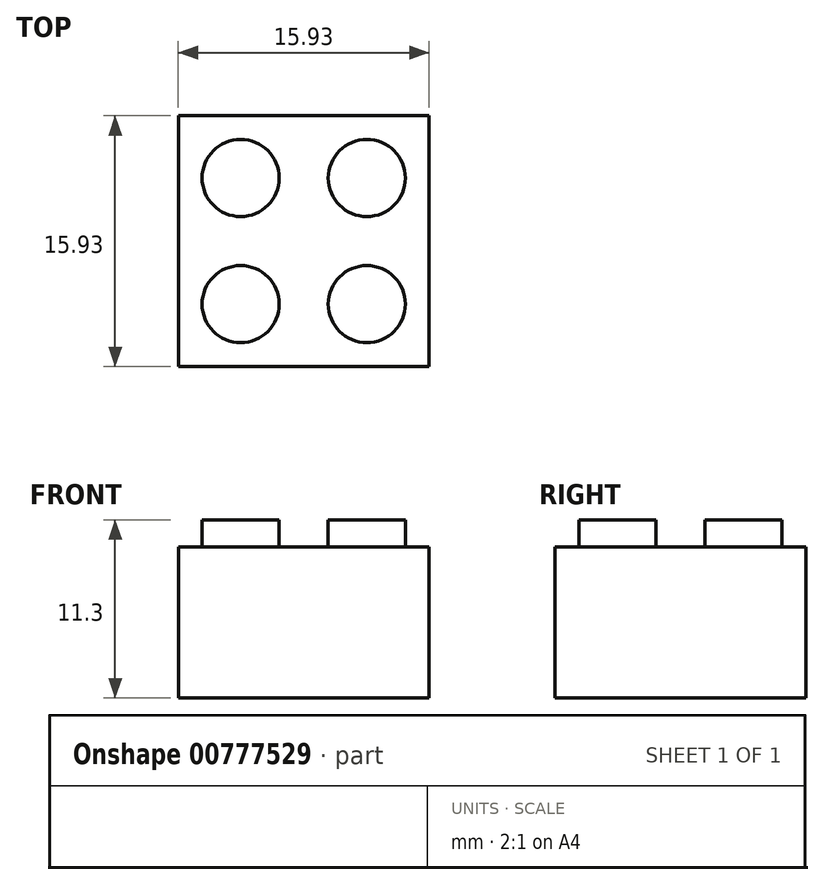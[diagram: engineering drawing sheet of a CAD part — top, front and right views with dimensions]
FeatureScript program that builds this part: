
annotation { "Feature Type Name" : "Feature", "Feature Type Description" : "" }
export const myFeature = defineFeature(function(context is Context, id is Id, definition is map)
    precondition{}
    {
        {
            var Q0;
            Q0=qCreatedBy(makeId("Top.planeOp"),FACE);
            var sketch = newSketch(context, id + "F0", { "sketchPlane" : qUnion([Q0])});
            skLineSegment(sketch, "E0.bottom", {"start": v(0, 0) * mm, "end": v(-15.93, 0) * mm});
            skLineSegment(sketch, "E0.top", {"start": v(0, 15.93) * mm, "end": v(-15.93, 15.93) * mm});
            skLineSegment(sketch, "E0.left", {"start": v(0, 0) * mm, "end": v(0, 15.93) * mm});
            skLineSegment(sketch, "E0.right", {"start": v(-15.93, 0) * mm, "end": v(-15.93, 15.93) * mm});
            skLineSegment(sketch, "E1", {"start": v(1.44, 0) * mm, "end": v(1.44, 3.96) * mm, "construction": true});
            skLineSegment(sketch, "E2", {"start": v(1.44, 3.96) * mm, "end": v(1.44, 11.97) * mm, "construction": true});
            skLineSegment(sketch, "E3", {"start": v(1.44, 11.97) * mm, "end": v(1.44, 15.93) * mm, "construction": true});
            skLineSegment(sketch, "E4", {"start": v(-15.94, -2.24) * mm, "end": v(-11.98, -2.24) * mm, "construction": true});
            skLineSegment(sketch, "E5", {"start": v(-11.98, -2.24) * mm, "end": v(-3.97, -2.24) * mm, "construction": true});
            skLineSegment(sketch, "E6", {"start": v(-3.97, -2.24) * mm, "end": v(-0.01, -2.24) * mm, "construction": true});
            skSolve(sketch);
        }
        {
            var Q0;
            Q0=makeQuery(id+"F0.imprint","IMPRINT",FACE,{"disambiguationData":[TD([[makeQuery(id+"F0.imprint","IMPRINT",EDGE,{"derivedFrom":sQuery(id+"F0.wireOp",EDGE,"E0.bottom")}),-1.0]])]});
            var Q1;
            Q1=sQuery(id+"F0.wireOp",EDGE,"530b2f17-7b4d-467d-ae32-fa93eb3b95f9");
            var Q2;
            Q2=sQuery(id+"F0.wireOp",EDGE,"9orbX4un-kg6Y-8ypP-M3kx-j9l8BkMfJr51");
            var Q3;
            Q3=sQuery(id+"F0.wireOp",EDGE,"hj133GTl-0r54-wE85-V2xD-Qsv4T7gERf85");
            extrude(context, id + "F1", {"entities" : qUnion([Q0]), "surfaceOperationType" : NewSurfaceOperationType.ADD, "surfaceEntities" : qUnion([Q1, Q2, Q3]), "depth" : 9.6 * mm, "offsetDistance" : 25 * mm});
        }
        {
            var Q0;
            Q0=makeQuery(id+"F1.opExtrude","CAP_FACE",FACE,{"disambiguationData":[OSD([sQuery(id+"F0.wireOp",EDGE,"E0.bottom"),sQuery(id+"F0.wireOp",EDGE,"E0.top"),sQuery(id+"F0.wireOp",EDGE,"E0.left"),sQuery(id+"F0.wireOp",EDGE,"E0.right")])],"isStart":false});
            var sketch = newSketch(context, id + "F2", { "sketchPlane" : qUnion([Q0])});
            skCircle(sketch, "E7", {"center": v(-3.96, 3.96) * mm, "radius": 2.45 * mm});
            skLineSegment(sketch, "E8", {"start": v(1.38, 0) * mm, "end": v(1.38, 3.96) * mm, "construction": true});
            skLineSegment(sketch, "E9", {"start": v(1.38, 3.96) * mm, "end": v(1.38, 11.97) * mm, "construction": true});
            skLineSegment(sketch, "E10", {"start": v(1.38, 11.97) * mm, "end": v(1.38, 15.93) * mm, "construction": true});
            skLineSegment(sketch, "E11", {"start": v(-15.93, -1.64) * mm, "end": v(-11.97, -1.64) * mm, "construction": true});
            skLineSegment(sketch, "E12", {"start": v(-11.97, -1.64) * mm, "end": v(-3.96, -1.64) * mm, "construction": true});
            skLineSegment(sketch, "E13", {"start": v(-3.96, -1.64) * mm, "end": v(0, -1.64) * mm, "construction": true});
            skCircle(sketch, "E14", {"center": v(-11.97, 3.96) * mm, "radius": 2.45 * mm});
            skCircle(sketch, "E15", {"center": v(-3.96, 11.97) * mm, "radius": 2.45 * mm});
            skCircle(sketch, "E16", {"center": v(-11.97, 11.97) * mm, "radius": 2.45 * mm});
            skSolve(sketch);
        }
        {
            var Q0;
            Q0=makeQuery(id+"F2.imprint","IMPRINT",FACE,{"disambiguationData":[TD([[makeQuery(id+"F2.imprint","IMPRINT",EDGE,{"derivedFrom":sQuery(id+"F2.wireOp",EDGE,"E7")}),1.0]])]});
            var Q1;
            Q1=makeQuery(id+"F2.imprint","IMPRINT",FACE,{"disambiguationData":[TD([[makeQuery(id+"F2.imprint","IMPRINT",EDGE,{"derivedFrom":sQuery(id+"F2.wireOp",EDGE,"E15")}),1.0]])]});
            var Q2;
            Q2=makeQuery(id+"F2.imprint","IMPRINT",FACE,{"disambiguationData":[TD([[makeQuery(id+"F2.imprint","IMPRINT",EDGE,{"derivedFrom":sQuery(id+"F2.wireOp",EDGE,"E16")}),1.0]])]});
            var Q3;
            Q3=makeQuery(id+"F2.imprint","IMPRINT",FACE,{"disambiguationData":[TD([[makeQuery(id+"F2.imprint","IMPRINT",EDGE,{"derivedFrom":sQuery(id+"F2.wireOp",EDGE,"E14")}),1.0]])]});
            extrude(context, id + "F3", {"entities" : qUnion([Q0, Q1, Q2, Q3]), "operationType" : NewBodyOperationType.ADD, "depth" : 1.7 * mm, "offsetDistance" : 25 * mm});
        }
    });
